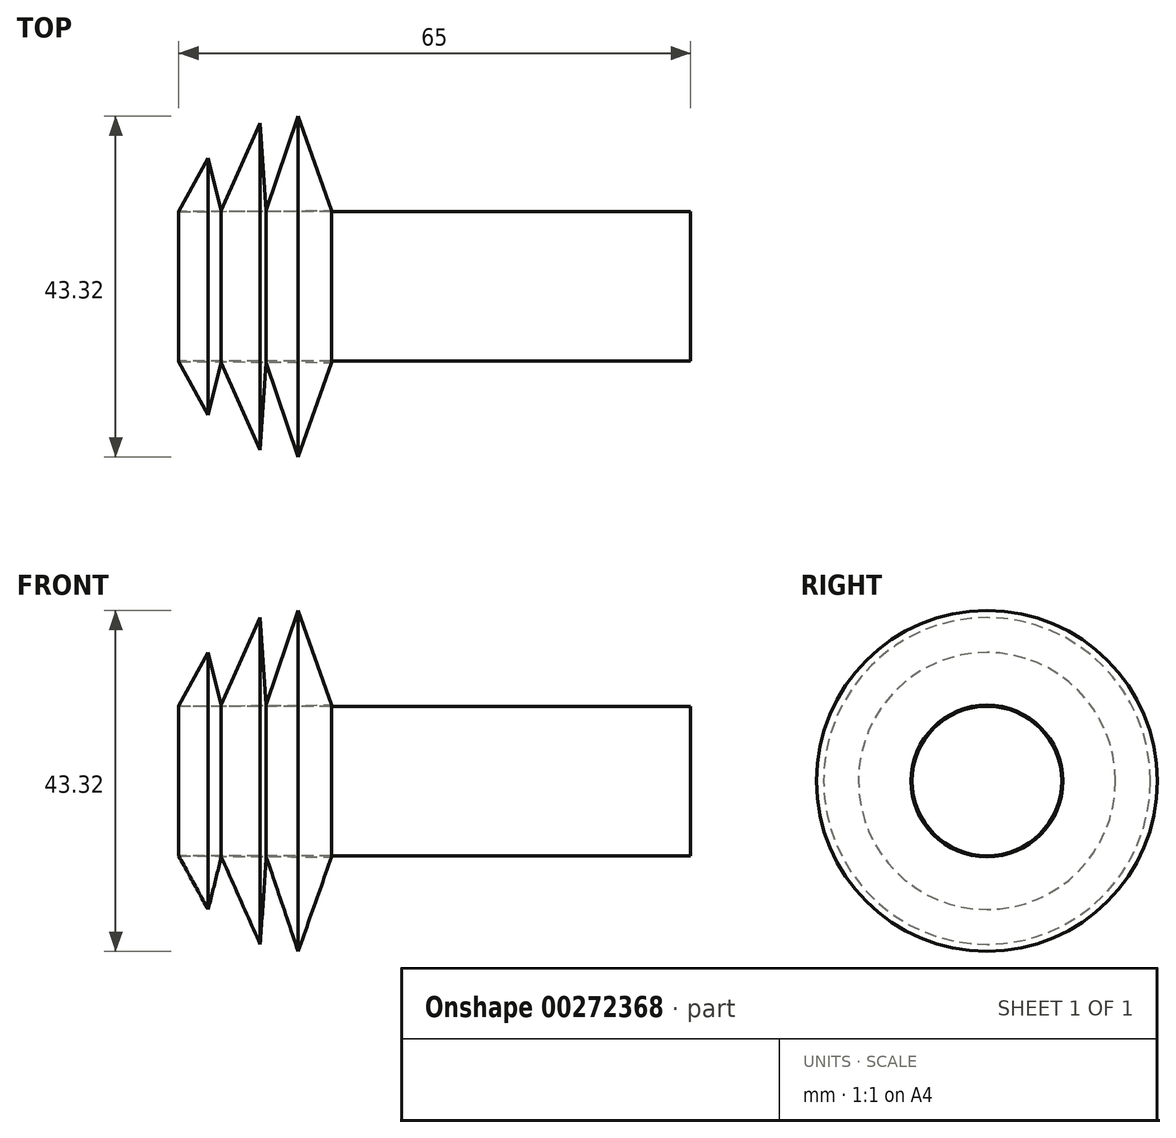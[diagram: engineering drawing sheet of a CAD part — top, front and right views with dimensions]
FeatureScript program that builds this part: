
annotation { "Feature Type Name" : "Feature", "Feature Type Description" : "" }
export const myFeature = defineFeature(function(context is Context, id is Id, definition is map)
    precondition{}
    {
        {
            var Q0;
            Q0=qCreatedBy(makeId("Right.planeOp"),FACE);
            var sketch = newSketch(context, id + "F0", { "sketchPlane" : qUnion([Q0])});
            skCircle(sketch, "E0", {"center": v(0, 0) * mm, "radius": 9.5 * mm});
            skSolve(sketch);
        }
        {
            var Q0;
            Q0=makeQuery(id+"F0.imprint","IMPRINT",FACE,{"disambiguationData":[TD([[makeQuery(id+"F0.imprint","IMPRINT",EDGE,{"derivedFrom":sQuery(id+"F0.wireOp",EDGE,"E0")}),1.0]])]});
            extrude(context, id + "F1", {"entities" : qUnion([Q0]), "depth" : 65 * mm});
        }
        {
            var Q0;
            Q0=qCreatedBy(makeId("Front.planeOp"),FACE);
            var sketch = newSketch(context, id + "F2", { "sketchPlane" : qUnion([Q0])});
            skLineSegment(sketch, "E1", {"start": v(0, 9.51) * mm, "end": v(3.73, 16.32) * mm});
            skLineSegment(sketch, "E2", {"start": v(3.73, 16.32) * mm, "end": v(5.4, 9.64) * mm});
            skLineSegment(sketch, "E3", {"start": v(5.4, 9.64) * mm, "end": v(10.35, 20.76) * mm});
            skLineSegment(sketch, "E4", {"start": v(10.35, 20.76) * mm, "end": v(11.12, 9.64) * mm});
            skLineSegment(sketch, "E5", {"start": v(11.12, 9.64) * mm, "end": v(15.17, 21.66) * mm});
            skLineSegment(sketch, "E6", {"start": v(15.17, 21.66) * mm, "end": v(19.4, 9.64) * mm});
            skLineSegment(sketch, "E7", {"start": v(19.4, 9.64) * mm, "end": v(0, 9.51) * mm});
            skSolve(sketch);
        }
        {
            var Q0;
            Q0 = qSketchRegion(id + "F2", true);
            var Q1;
            Q1=makeQuery(id+"F1.opExtrude","SWEPT_FACE",FACE,{"disambiguationData":[OSD([sQuery(id+"F0.wireOp",EDGE,"E0")])]});
            revolve(context, id + "F3", {"entities" : qUnion([Q0]), "axis" : qUnion([Q1]), "revolveType" : RevolveType.FULL});
        }
    });
